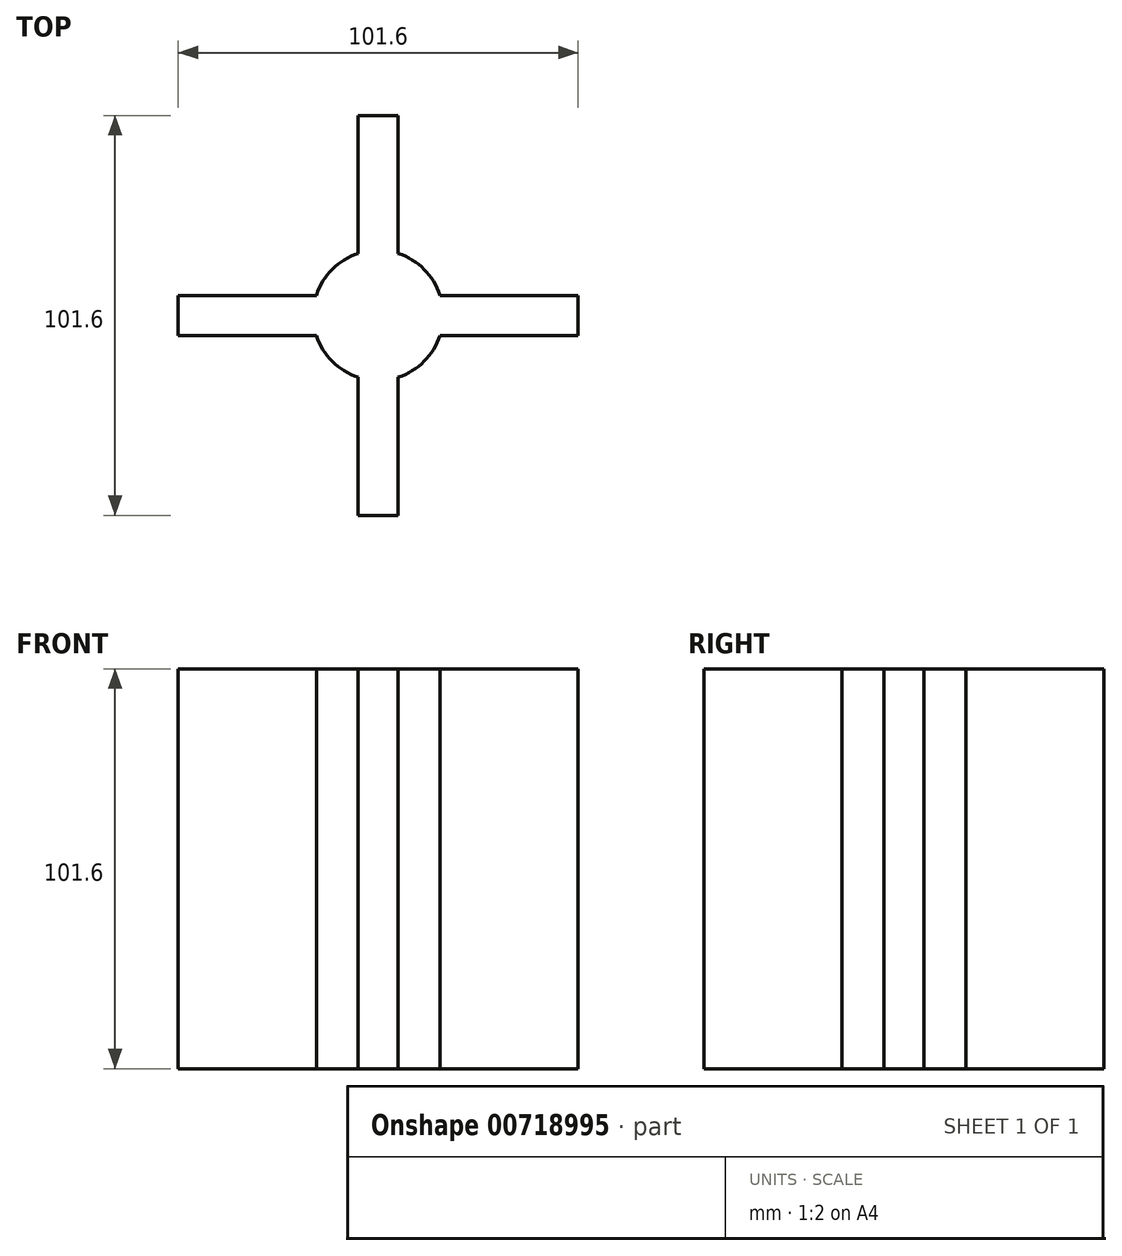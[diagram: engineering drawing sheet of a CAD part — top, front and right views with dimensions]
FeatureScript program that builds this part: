
annotation { "Feature Type Name" : "Feature", "Feature Type Description" : "" }
export const myFeature = defineFeature(function(context is Context, id is Id, definition is map)
    precondition{}
    {
        {
            var Q0;
            Q0=qCreatedBy(makeId("Top.planeOp"),FACE);
            var sketch = newSketch(context, id + "F0", { "sketchPlane" : qUnion([Q0])});
            skLineSegment(sketch, "E0.bottom", {"start": v(-5.08, 50.8) * mm, "end": v(5.08, 50.8) * mm});
            skLineSegment(sketch, "E0.top", {"start": v(-5.08, -50.8) * mm, "end": v(5.08, -50.8) * mm});
            skLineSegment(sketch, "E0.left", {"start": v(-5.08, 50.8) * mm, "end": v(-5.08, 15.7) * mm});
            skLineSegment(sketch, "E0.right", {"start": v(5.08, 50.8) * mm, "end": v(5.08, 15.7) * mm});
            skLineSegment(sketch, "E1.bottom", {"start": v(50.8, 5.08) * mm, "end": v(15.7, 5.08) * mm});
            skLineSegment(sketch, "E1.top", {"start": v(50.8, -5.08) * mm, "end": v(15.7, -5.08) * mm});
            skLineSegment(sketch, "E1.left", {"start": v(50.8, 5.08) * mm, "end": v(50.8, -5.08) * mm});
            skLineSegment(sketch, "E1.right", {"start": v(-50.8, 5.08) * mm, "end": v(-50.8, -5.08) * mm});
            skArc(sketch, "E2", {"start": v(-5.08, 15.7) * mm, "mid": v(-11.67, 11.67) * mm, "end": v(-15.7, 5.08) * mm});
            skArc(sketch, "E3.trimOffspring", {"start": v(15.7, 5.08) * mm, "mid": v(11.67, 11.67) * mm, "end": v(5.08, 15.7) * mm});
            skArc(sketch, "E4.trimOffspring", {"start": v(5.08, -15.7) * mm, "mid": v(11.67, -11.67) * mm, "end": v(15.7, -5.08) * mm});
            skArc(sketch, "E5.trimOffspring", {"start": v(-15.7, -5.08) * mm, "mid": v(-11.67, -11.67) * mm, "end": v(-5.08, -15.7) * mm});
            skLineSegment(sketch, "E6.trimOffspring", {"start": v(-15.7, -5.08) * mm, "end": v(-50.8, -5.08) * mm});
            skLineSegment(sketch, "E7.trimOffspring", {"start": v(-5.08, -15.7) * mm, "end": v(-5.08, -50.8) * mm});
            skLineSegment(sketch, "E8.trimOffspring", {"start": v(-15.7, 5.08) * mm, "end": v(-50.8, 5.08) * mm});
            skLineSegment(sketch, "E9.trimOffspring", {"start": v(5.08, -15.7) * mm, "end": v(5.08, -50.8) * mm});
            skSolve(sketch);
        }
        {
            var Q0;
            Q0 = qSketchRegion(id + "F0", true);
            extrude(context, id + "F1", {"entities" : qUnion([Q0]), "depth" : 101.6 * mm, "offsetDistance" : 25.4 * mm});
        }
    });
